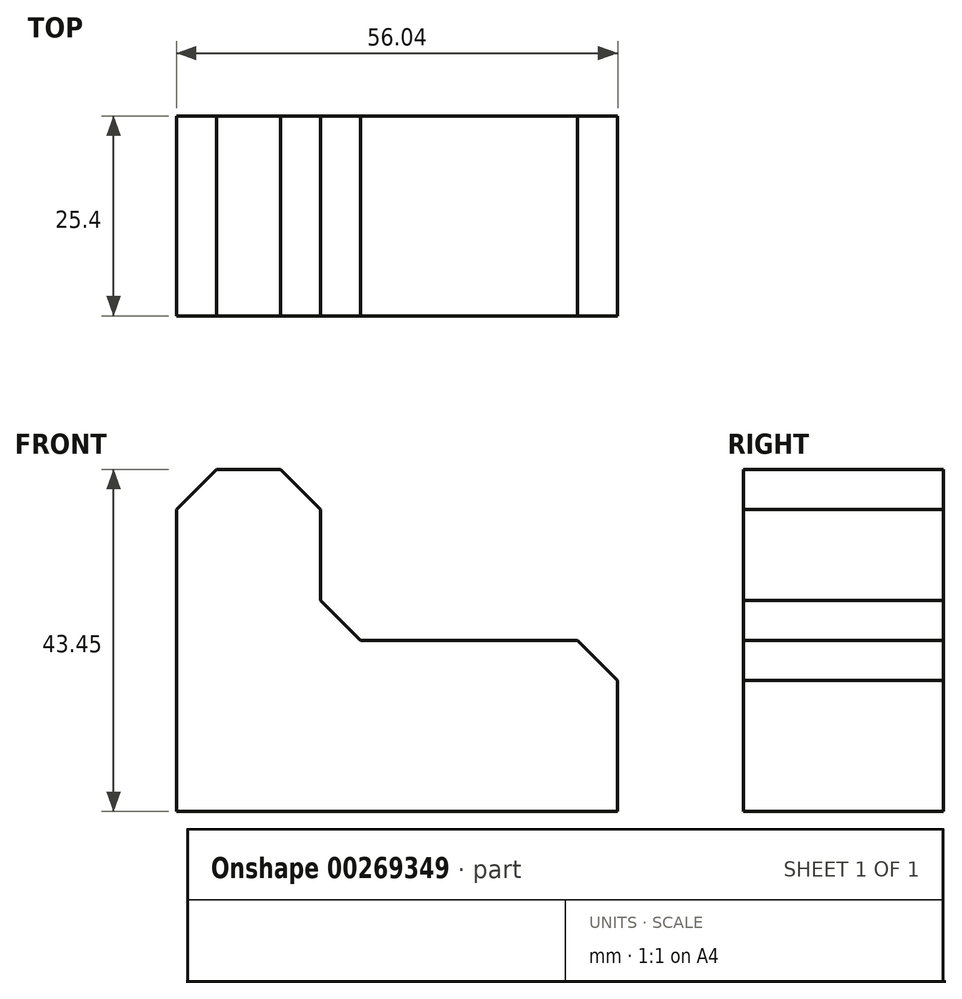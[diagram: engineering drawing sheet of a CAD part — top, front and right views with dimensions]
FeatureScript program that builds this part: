
annotation { "Feature Type Name" : "Feature", "Feature Type Description" : "" }
export const myFeature = defineFeature(function(context is Context, id is Id, definition is map)
    precondition{}
    {
        {
            var Q0;
            Q0=qCreatedBy(makeId("Front.planeOp"),FACE);
            var sketch = newSketch(context, id + "F0", { "sketchPlane" : qUnion([Q0])});
            skLineSegment(sketch, "E0.bottom", {"start": v(0, 0) * mm, "end": v(56.04, 0) * mm});
            skLineSegment(sketch, "E0.top", {"start": v(0, 43.45) * mm, "end": v(18.28, 43.45) * mm});
            skLineSegment(sketch, "E0.left", {"start": v(0, 0) * mm, "end": v(0, 43.45) * mm});
            skLineSegment(sketch, "E0.right", {"start": v(56.04, 0) * mm, "end": v(56.04, 21.73) * mm});
            skLineSegment(sketch, "E1.top", {"start": v(18.28, 21.73) * mm, "end": v(56.04, 21.73) * mm});
            skLineSegment(sketch, "E1.left", {"start": v(18.28, 43.45) * mm, "end": v(18.28, 21.73) * mm});
            skPoint(sketch, "E2.orphan", {"position": v(56.04, 43.45) * mm});
            skSolve(sketch);
        }
        {
            var Q0;
            Q0 = qSketchRegion(id + "F0", true);
            extrude(context, id + "F1", {"entities" : qUnion([Q0]), "depth" : 25.4 * mm});
        }
        {
            var Q0;
            Q0=makeQuery(id+"F1.opExtrude","SWEPT_EDGE",EDGE,{"disambiguationData":[OSD([sQuery(id+"F0.wireOp",EDGE,"E0.right"),sQuery(id+"F0.wireOp",EDGE,"E1.top")])]});
            chamfer(context, id + "F2", {"entities" : qUnion([Q0]), "width" : 5.08 * mm, "tangentPropagation" : true});
        }
        {
            var Q0;
            Q0=makeQuery(id+"F1.opExtrude","SWEPT_EDGE",EDGE,{"disambiguationData":[OSD([sQuery(id+"F0.wireOp",EDGE,"E0.top"),sQuery(id+"F0.wireOp",EDGE,"E1.left")])]});
            var Q1;
            Q1=makeQuery(id+"F1.opExtrude","SWEPT_EDGE",EDGE,{"disambiguationData":[OSD([sQuery(id+"F0.wireOp",EDGE,"E1.top"),sQuery(id+"F0.wireOp",EDGE,"E1.left")])]});
            var Q2;
            Q2=makeQuery(id+"F1.opExtrude","SWEPT_EDGE",EDGE,{"disambiguationData":[OSD([sQuery(id+"F0.wireOp",EDGE,"E0.top"),sQuery(id+"F0.wireOp",EDGE,"E0.left")])]});
            chamfer(context, id + "F3", {"entities" : qUnion([Q0, Q1, Q2]), "width" : 5.08 * mm, "tangentPropagation" : true});
        }
    });
